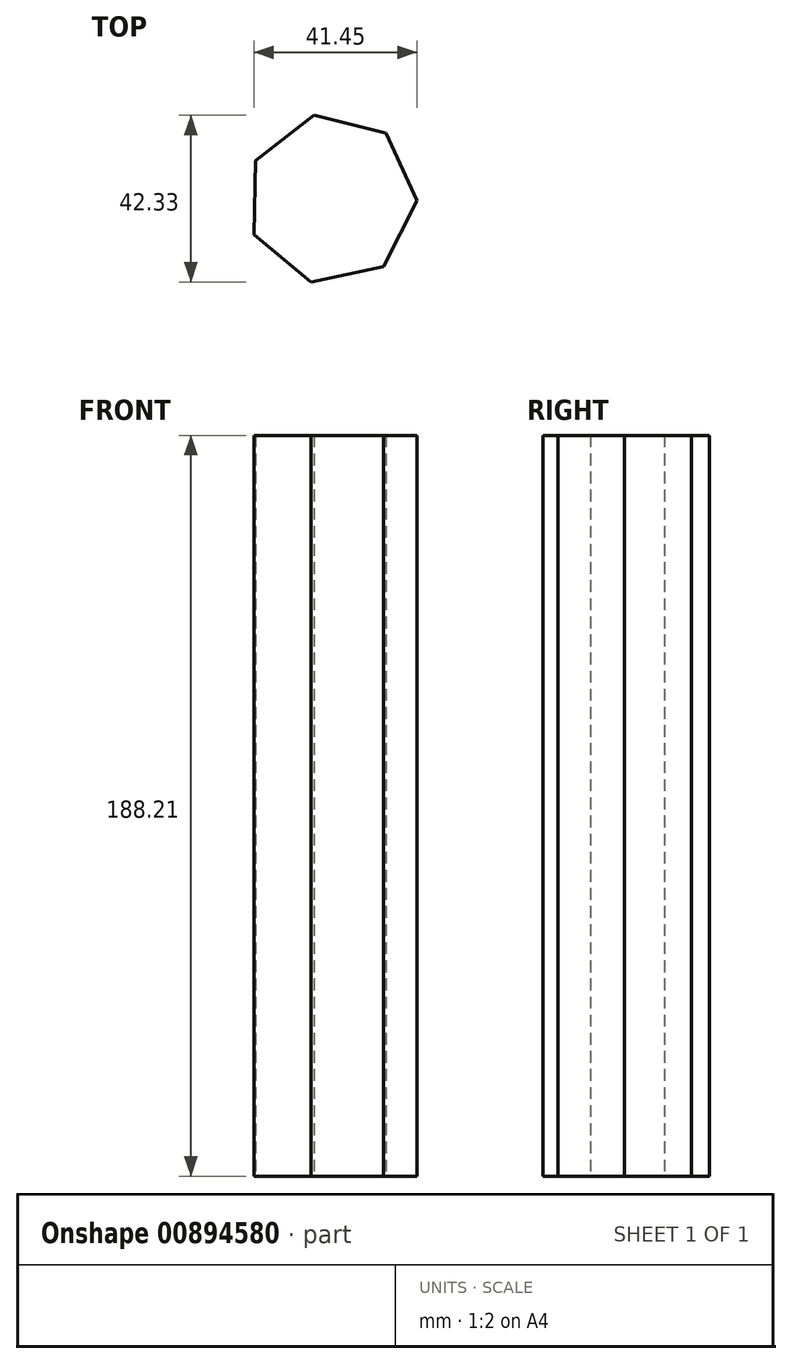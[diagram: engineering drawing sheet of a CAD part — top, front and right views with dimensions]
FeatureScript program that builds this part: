
annotation { "Feature Type Name" : "Feature", "Feature Type Description" : "" }
export const myFeature = defineFeature(function(context is Context, id is Id, definition is map)
    precondition{}
    {
        {
            var Q0;
            Q0=qCreatedBy(makeId("Top.planeOp"),FACE);
            var sketch = newSketch(context, id + "F0", { "sketchPlane" : qUnion([Q0])});
            skCircle(sketch, "E0.cCircle", {"center": v(-49.77, 30.05) * mm, "radius": 19.56 * mm, "construction": true});
            skLineSegment(sketch, "E0.0", {"start": v(-36.57, 12.82) * mm, "end": v(-55, 8.98) * mm});
            skLineSegment(sketch, "E0.1", {"start": v(-55, 8.98) * mm, "end": v(-69.5, 21.01) * mm});
            skLineSegment(sketch, "E0.2", {"start": v(-69.5, 21.01) * mm, "end": v(-69.14, 39.85) * mm});
            skLineSegment(sketch, "E0.3", {"start": v(-69.14, 39.85) * mm, "end": v(-54.19, 51.3) * mm});
            skLineSegment(sketch, "E0.4", {"start": v(-54.19, 51.3) * mm, "end": v(-35.9, 46.76) * mm});
            skLineSegment(sketch, "E0.5", {"start": v(-35.9, 46.76) * mm, "end": v(-28.06, 29.63) * mm});
            skLineSegment(sketch, "E0.6", {"start": v(-28.06, 29.63) * mm, "end": v(-36.57, 12.82) * mm});
            skPoint(sketch, "E0.0.midPoint", {"position": v(-45.79, 10.9) * mm});
            skFitSpline(sketch, "E1", {"points": [v(-75.93, 8.63) * mm, v(-57.16, 5.4) * mm, v(-36.69, -5.4) * mm, v(-19.24, -8.44) * mm, v(32.14, -11.47) * mm, v(46.36, -21.14) * mm, v(62.28, -25.12) * mm, v(76.31, -27.59) * mm], "startDerivative": vector(137.96, -8.38) * mm, "endDerivative": vector(115.9, -22.26) * mm});
            skSolve(sketch);
        }
        {
            var Q0;
            Q0=makeQuery(id+"F0.imprint","IMPRINT",FACE,{"disambiguationData":[TD([[makeQuery(id+"F0.imprint","IMPRINT",EDGE,{"derivedFrom":sQuery(id+"F0.wireOp",EDGE,"E0.0")}),-1.0]])]});
            extrude(context, id + "F1", {"entities" : qUnion([Q0]), "depth" : 188.21 * mm, "offsetDistance" : 25.4 * mm});
        }
    });
